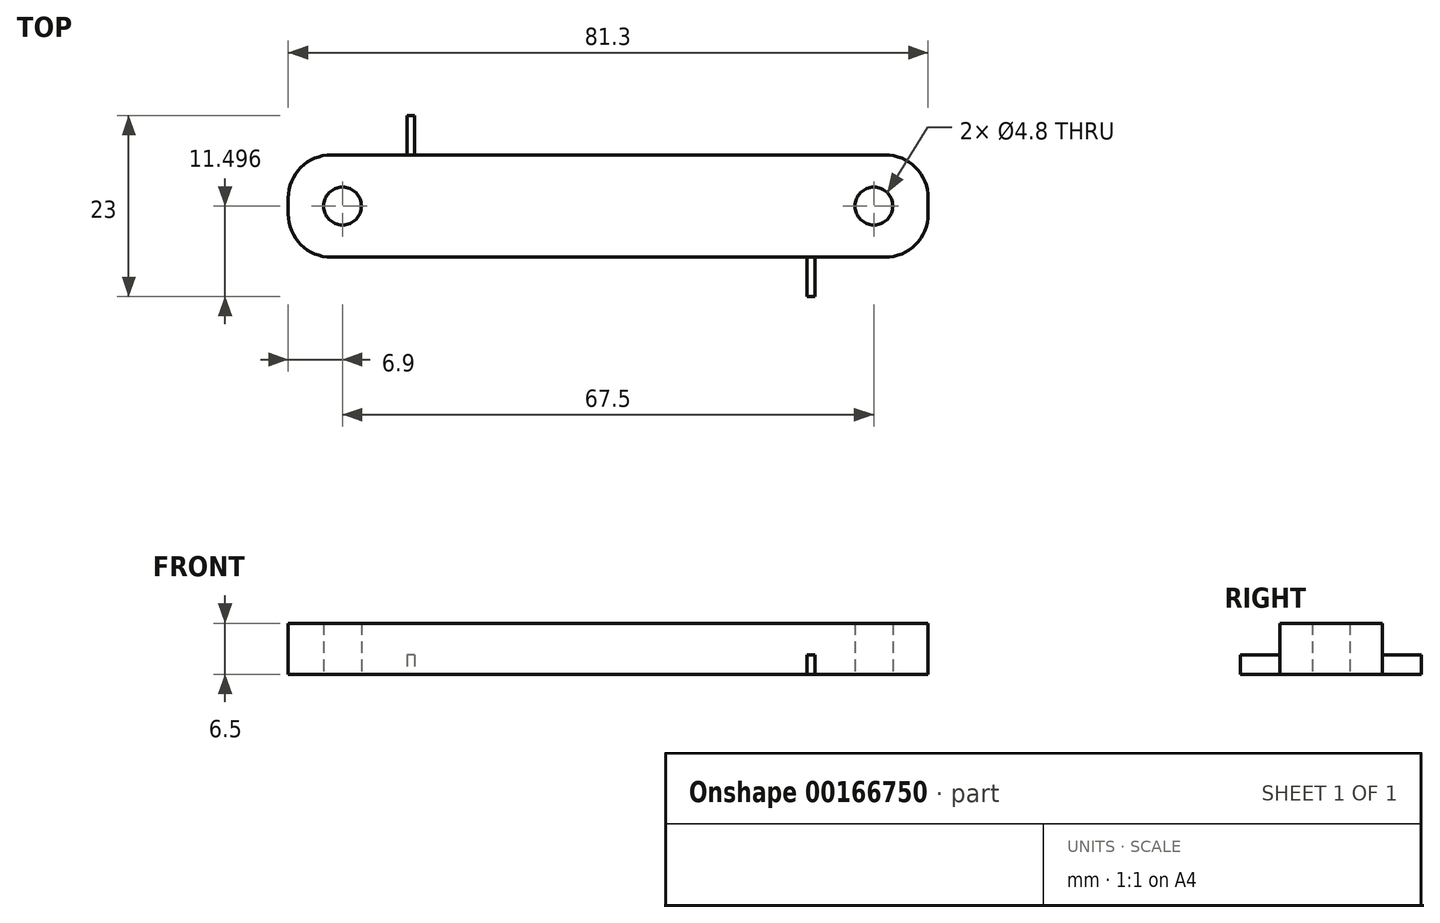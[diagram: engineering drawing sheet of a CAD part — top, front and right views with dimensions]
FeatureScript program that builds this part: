
annotation { "Feature Type Name" : "Feature", "Feature Type Description" : "" }
export const myFeature = defineFeature(function(context is Context, id is Id, definition is map)
    precondition{}
    {
        {
            var Q0;
            Q0=qCreatedBy(makeId("Top.planeOp"),FACE);
            var sketch = newSketch(context, id + "F0", { "sketchPlane" : qUnion([Q0])});
            skLineSegment(sketch, "E0.bottom", {"start": v(-40.65, 9.12) * mm, "end": v(40.65, 9.12) * mm});
            skLineSegment(sketch, "E0.top", {"start": v(-40.65, -3.88) * mm, "end": v(40.65, -3.88) * mm});
            skLineSegment(sketch, "E0.left", {"start": v(-40.65, 9.12) * mm, "end": v(-40.65, -3.88) * mm});
            skLineSegment(sketch, "E0.right", {"start": v(40.65, 9.12) * mm, "end": v(40.65, -3.88) * mm});
            skCircle(sketch, "E1", {"center": v(33.75, 2.62) * mm, "radius": 2.4 * mm});
            skCircle(sketch, "E2.MirrorC", {"center": v(-33.75, 2.62) * mm, "radius": 2.4 * mm});
            skSolve(sketch);
        }
        {
            var Q0;
            Q0=makeQuery(id+"F0.imprint","IMPRINT",FACE,{"disambiguationData":[TD([[makeQuery(id+"F0.imprint","IMPRINT",EDGE,{"derivedFrom":sQuery(id+"F0.wireOp",EDGE,"E0.bottom")}),-1.0]])]});
            extrude(context, id + "F1", {"entities" : qUnion([Q0]), "offsetDistance" : 25 * mm, "depth" : 6.5 * mm});
        }
        {
            var Q0;
            Q0=makeQuery(id+"F1.opExtrude","SWEPT_EDGE",EDGE,{"disambiguationData":[OSD([sQuery(id+"F0.wireOp",EDGE,"E0.bottom"),sQuery(id+"F0.wireOp",EDGE,"E0.left")])]});
            var Q1;
            Q1=makeQuery(id+"F1.opExtrude","SWEPT_EDGE",EDGE,{"disambiguationData":[OSD([sQuery(id+"F0.wireOp",EDGE,"E0.top"),sQuery(id+"F0.wireOp",EDGE,"E0.left")])]});
            var Q2;
            Q2=makeQuery(id+"F1.opExtrude","SWEPT_EDGE",EDGE,{"disambiguationData":[OSD([sQuery(id+"F0.wireOp",EDGE,"E0.top"),sQuery(id+"F0.wireOp",EDGE,"E0.right")])]});
            var Q3;
            Q3=makeQuery(id+"F1.opExtrude","SWEPT_EDGE",EDGE,{"disambiguationData":[OSD([sQuery(id+"F0.wireOp",EDGE,"E0.bottom"),sQuery(id+"F0.wireOp",EDGE,"E0.right")])]});
            fillet(context, id + "F2", {"entities" : qUnion([Q0, Q1, Q2, Q3]), "radius" : 5.5 * mm, "tangentPropagation" : true, "allowEdgeOverflow" : false});
        }
        {
            var Q0;
            Q0=makeQuery(id+"F1.opExtrude","SWEPT_FACE",FACE,{"disambiguationData":[OSD([sQuery(id+"F0.wireOp",EDGE,"E0.top")])]});
            var sketch = newSketch(context, id + "F3", { "sketchPlane" : qUnion([Q0])});
            skLineSegment(sketch, "E3.bottom", {"start": v(25.28, 2.5) * mm, "end": v(26.28, 2.5) * mm});
            skLineSegment(sketch, "E3.top", {"start": v(25.28, 0) * mm, "end": v(26.28, 0) * mm});
            skLineSegment(sketch, "E3.left", {"start": v(25.28, 2.5) * mm, "end": v(25.28, 0) * mm});
            skLineSegment(sketch, "E3.right", {"start": v(26.28, 2.5) * mm, "end": v(26.28, 0) * mm});
            skSolve(sketch);
        }
        {
            var Q0;
            Q0 = qSketchRegion(id + "F3", true);
            extrude(context, id + "F4", {"entities" : qUnion([Q0]), "operationType" : NewBodyOperationType.ADD, "depth" : 5 * mm});
        }
        {
            var Q0;
            Q0=makeQuery(id+"F1.opExtrude","SWEPT_FACE",FACE,{"disambiguationData":[OSD([sQuery(id+"F0.wireOp",EDGE,"E0.bottom")])]});
            var sketch = newSketch(context, id + "F5", { "sketchPlane" : qUnion([Q0])});
            skLineSegment(sketch, "E4.bottom", {"start": v(24.57, 2.5) * mm, "end": v(25.57, 2.5) * mm});
            skLineSegment(sketch, "E4.top", {"start": v(24.57, 0) * mm, "end": v(25.57, 0) * mm});
            skLineSegment(sketch, "E4.left", {"start": v(24.57, 2.5) * mm, "end": v(24.57, 0) * mm});
            skLineSegment(sketch, "E4.right", {"start": v(25.57, 2.5) * mm, "end": v(25.57, 0) * mm});
            skSolve(sketch);
        }
        {
            var Q0;
            Q0 = qSketchRegion(id + "F5", true);
            extrude(context, id + "F6", {"entities" : qUnion([Q0]), "operationType" : NewBodyOperationType.ADD, "depth" : 5 * mm});
        }
    });
